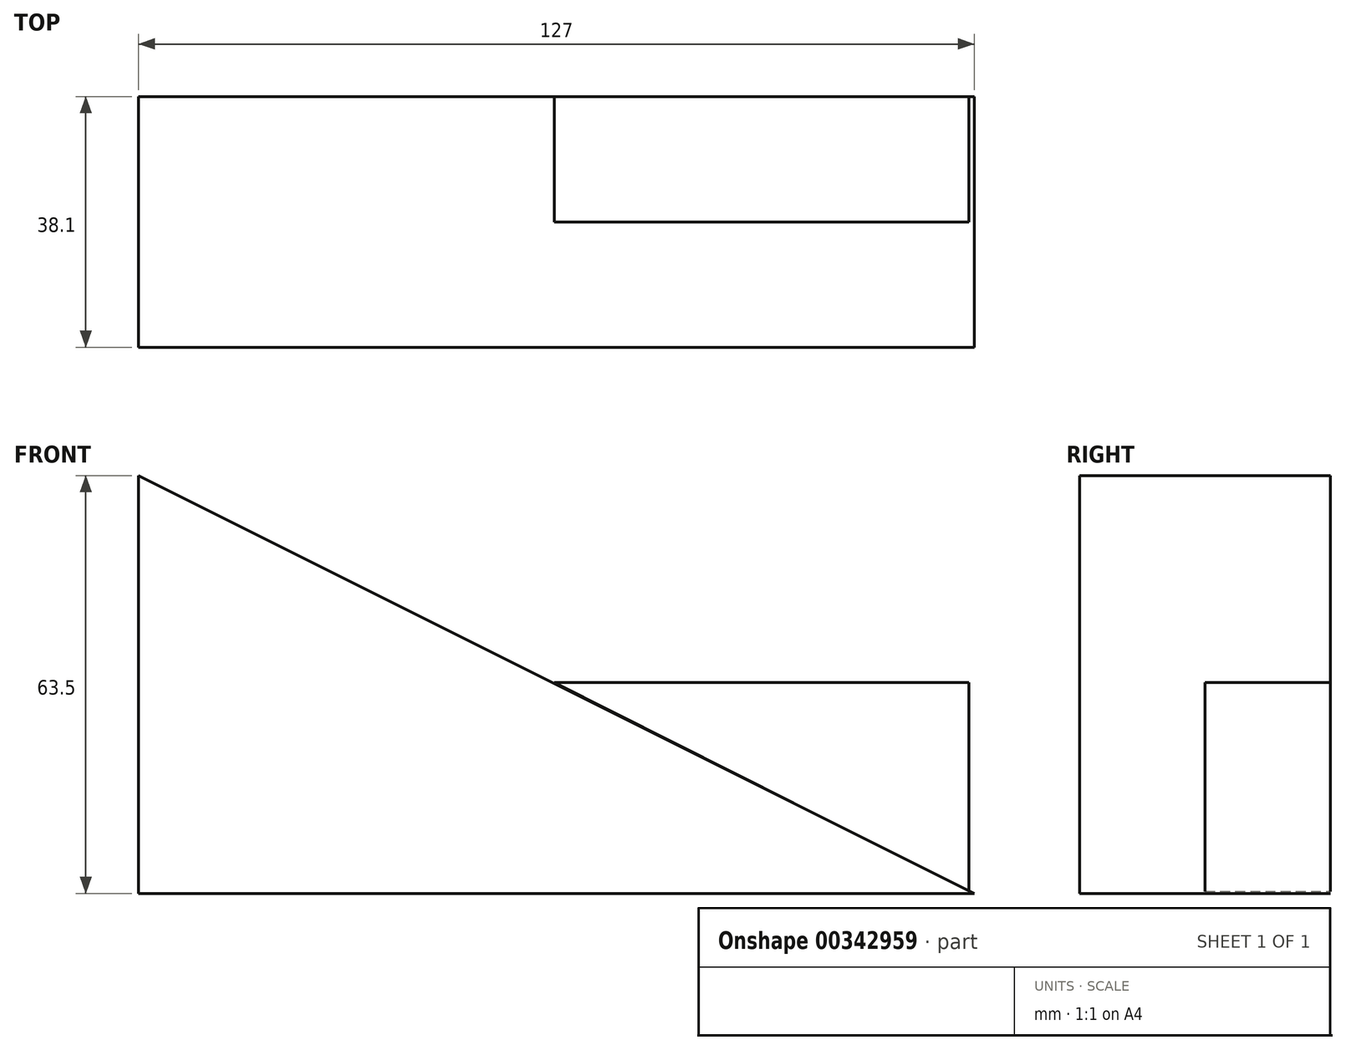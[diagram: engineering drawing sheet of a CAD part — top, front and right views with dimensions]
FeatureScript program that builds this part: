
annotation { "Feature Type Name" : "Feature", "Feature Type Description" : "" }
export const myFeature = defineFeature(function(context is Context, id is Id, definition is map)
    precondition{}
    {
        {
            var Q0;
            Q0=qCreatedBy(makeId("Front.planeOp"),FACE);
            var sketch = newSketch(context, id + "F0", { "sketchPlane" : qUnion([Q0])});
            skLineSegment(sketch, "E0", {"start": v(-60, -45.62) * mm, "end": v(67, -45.62) * mm});
            skLineSegment(sketch, "E1", {"start": v(-60, -45.62) * mm, "end": v(-60, 17.88) * mm});
            skLineSegment(sketch, "E2", {"start": v(-60, 17.88) * mm, "end": v(67, -45.62) * mm});
            skSolve(sketch);
        }
        {
            var Q0;
            Q0 = qSketchRegion(id + "F0", true);
            extrude(context, id + "F1", {"entities" : qUnion([Q0]), "depth" : 38.1 * mm});
        }
        {
            var Q0;
            Q0=qCreatedBy(makeId("Front.planeOp"),FACE);
            var sketch = newSketch(context, id + "F2", { "sketchPlane" : qUnion([Q0])});
            skLineSegment(sketch, "E3", {"start": v(66.16, -45.31) * mm, "end": v(66.16, -13.56) * mm});
            skLineSegment(sketch, "E4", {"start": v(66.16, -13.56) * mm, "end": v(3.2, -13.56) * mm});
            skLineSegment(sketch, "E5", {"start": v(3.2, -13.56) * mm, "end": v(66.16, -45.31) * mm});
            skSolve(sketch);
        }
        {
            var Q0;
            Q0 = qSketchRegion(id + "F2", true);
            extrude(context, id + "F3", {"entities" : qUnion([Q0]), "depth" : 19.05 * mm});
        }
    });
